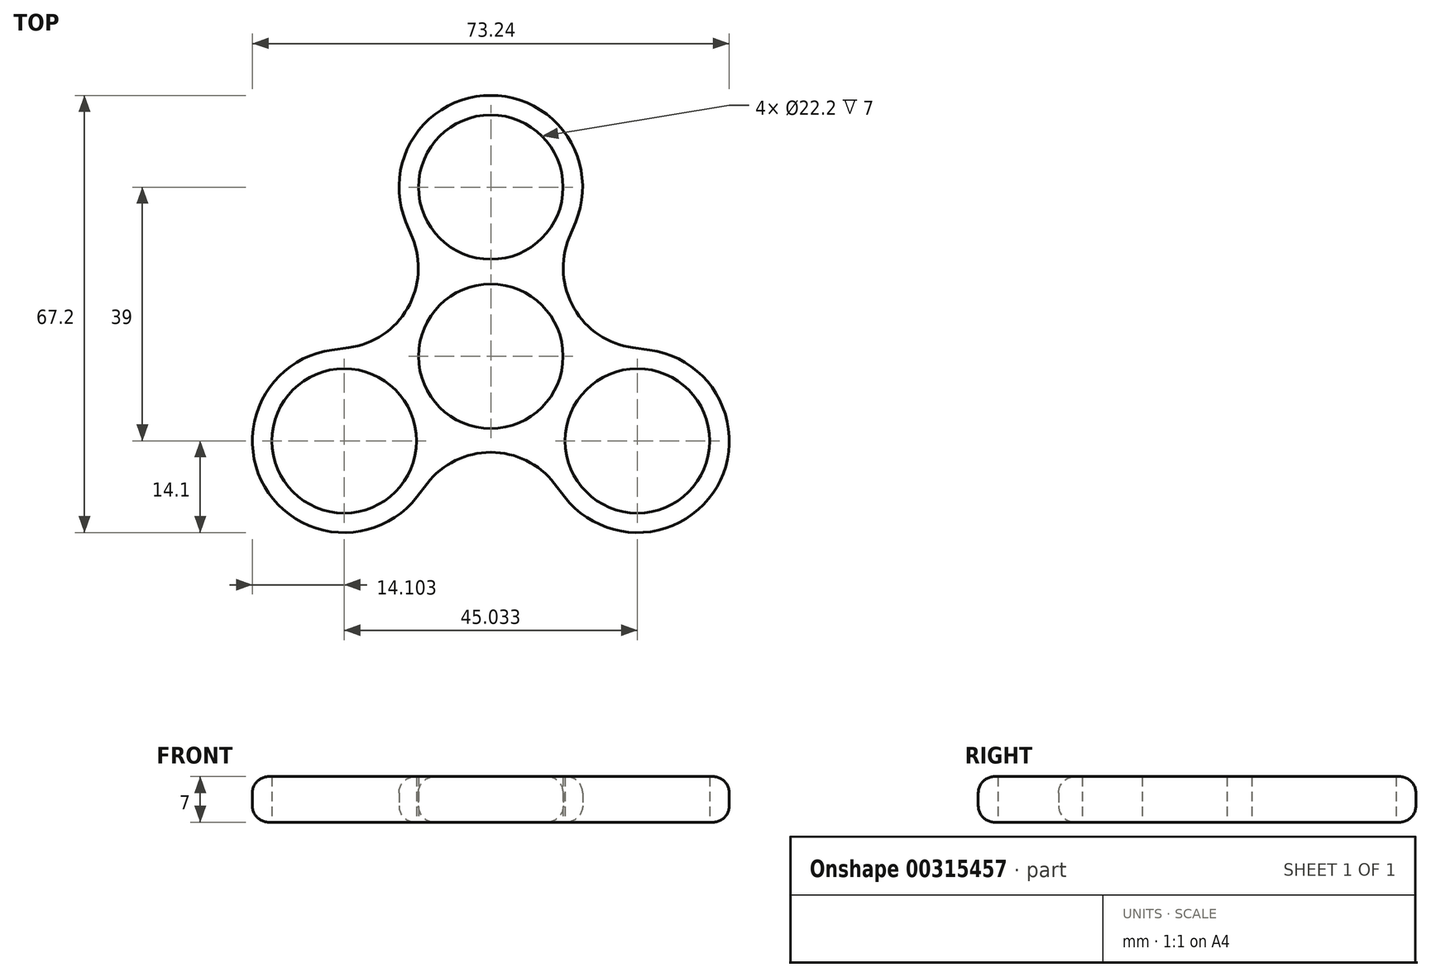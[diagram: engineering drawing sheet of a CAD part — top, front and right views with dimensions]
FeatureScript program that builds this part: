
annotation { "Feature Type Name" : "Feature", "Feature Type Description" : "" }
export const myFeature = defineFeature(function(context is Context, id is Id, definition is map)
    precondition{}
    {
        {
            var Q0;
            Q0=qCreatedBy(makeId("Top.planeOp"),FACE);
            var sketch = newSketch(context, id + "F0", { "sketchPlane" : qUnion([Q0])});
            skCircle(sketch, "E0", {"center": v(0, 0) * mm, "radius": 11.1 * mm});
            skCircle(sketch, "E1", {"center": v(0, 26) * mm, "radius": 11.1 * mm});
            skCircle(sketch, "E2", {"center": v(0, 26) * mm, "radius": 14.1 * mm});
            skLineSegment(sketch, "E3", {"start": v(0, -11.1) * mm, "end": v(-13.04, 20.64) * mm});
            skLineSegment(sketch, "E4", {"start": v(0, -11.1) * mm, "end": v(13.04, 20.64) * mm});
            skCircle(sketch, "E5.1.0", {"center": v(-22.52, -13) * mm, "radius": 14.1 * mm});
            skCircle(sketch, "E5.1.1", {"center": v(-22.52, -13) * mm, "radius": 11.1 * mm});
            skLineSegment(sketch, "E5.1.2", {"start": v(9.61, 5.55) * mm, "end": v(-11.35, -21.62) * mm});
            skLineSegment(sketch, "E5.1.3", {"start": v(9.61, 5.55) * mm, "end": v(-24.4, 0.97) * mm});
            skCircle(sketch, "E5.2.0", {"center": v(22.52, -13) * mm, "radius": 14.1 * mm});
            skCircle(sketch, "E5.2.1", {"center": v(22.52, -13) * mm, "radius": 11.1 * mm});
            skLineSegment(sketch, "E5.2.2", {"start": v(-9.61, 5.55) * mm, "end": v(24.4, 0.97) * mm});
            skLineSegment(sketch, "E5.2.3", {"start": v(-9.61, 5.55) * mm, "end": v(11.35, -21.62) * mm});
            skLineSegment(sketch, "E6", {"start": v(-12.21, 33.05) * mm, "end": v(-34.73, -5.95) * mm});
            skCircle(sketch, "E7", {"center": v(-23.47, 13.55) * mm, "radius": 12.34 * mm});
            skLineSegment(sketch, "E8", {"start": v(-22.52, -27.1) * mm, "end": v(22.52, -27.1) * mm});
            skLineSegment(sketch, "E9", {"start": v(34.73, -5.95) * mm, "end": v(12.21, 33.05) * mm});
            skCircle(sketch, "E10", {"center": v(23.47, 13.55) * mm, "radius": 12.34 * mm});
            skCircle(sketch, "E11", {"center": v(0, -27.1) * mm, "radius": 12.34 * mm});
            skSolve(sketch);
        }
        {
            var Q0;
            Q0=makeQuery(id+"F0.imprint","IMPRINT",FACE,{"disambiguationData":[TD([[makeQuery(id+"F0.imprint","IMPRINT",EDGE,{"derivedFrom":sQuery(id+"F0.wireOp",EDGE,"E1")}),-1.0]])]});
            var Q1;
            {var subQ4=sQuery(id+"F0.wireOp",EDGE,"E0");var subQ6=sQuery(id+"F0.wireOp",EDGE,"E4");var subQ8=makeQuery(id+"F0.imprint","INTERSECT",VERTEX,{"derivedFrom":[subQ4,subQ6]});Q1=makeQuery(id+"F0.imprint","IMPRINT",FACE,{"disambiguationData":[TD([[makeQuery(id+"F0.imprint","IMPRINT",EDGE,{"disambiguationData":[TD([[subQ8,-1.0]])],"derivedFrom":subQ4}),-1.0]])]});}
            var Q2;
            {var subQ1=sQuery(id+"F0.wireOp",EDGE,"E0");var subQ5=sQuery(id+"F0.wireOp",EDGE,"E3");var subQ6=makeQuery(id+"F0.imprint","INTERSECT",VERTEX,{"derivedFrom":[subQ1,subQ5]});Q2=makeQuery(id+"F0.imprint","IMPRINT",FACE,{"disambiguationData":[TD([[makeQuery(id+"F0.imprint","IMPRINT",EDGE,{"disambiguationData":[TD([[subQ6,-1.0]])],"derivedFrom":subQ5}),1.0]])]});}
            var Q3;
            {var subQ4=sQuery(id+"F0.wireOp",EDGE,"E0");var subQ6=sQuery(id+"F0.wireOp",EDGE,"E5.1.3");var subQ7=makeQuery(id+"F0.imprint","INTERSECT",VERTEX,{"derivedFrom":[subQ4,subQ6]});Q3=makeQuery(id+"F0.imprint","IMPRINT",FACE,{"disambiguationData":[TD([[makeQuery(id+"F0.imprint","IMPRINT",EDGE,{"disambiguationData":[TD([[subQ7,-1.0]])],"derivedFrom":subQ4}),-1.0]])]});}
            var Q4;
            Q4=makeQuery(id+"F0.imprint","IMPRINT",FACE,{"disambiguationData":[TD([[makeQuery(id+"F0.imprint","IMPRINT",EDGE,{"derivedFrom":sQuery(id+"F0.wireOp",EDGE,"E5.1.1")}),-1.0]])]});
            var Q5;
            {var subQ1=sQuery(id+"F0.wireOp",EDGE,"E0");var subQ5=sQuery(id+"F0.wireOp",EDGE,"E5.1.2");var subQ6=makeQuery(id+"F0.imprint","INTERSECT",VERTEX,{"derivedFrom":[subQ1,subQ5]});Q5=makeQuery(id+"F0.imprint","IMPRINT",FACE,{"disambiguationData":[TD([[makeQuery(id+"F0.imprint","IMPRINT",EDGE,{"disambiguationData":[TD([[subQ6,-1.0]])],"derivedFrom":subQ5}),1.0]])]});}
            var Q6;
            {var subQ0=sQuery(id+"F0.wireOp",EDGE,"E5.2.2");var subQ1=sQuery(id+"F0.wireOp",EDGE,"E0");var subQ2=makeQuery(id+"F0.imprint","INTERSECT",VERTEX,{"derivedFrom":[subQ1,subQ0]});Q6=makeQuery(id+"F0.imprint","IMPRINT",FACE,{"disambiguationData":[TD([[makeQuery(id+"F0.imprint","IMPRINT",EDGE,{"disambiguationData":[TD([[subQ2,1.0]])],"derivedFrom":subQ1}),-1.0]])]});}
            var Q7;
            Q7=makeQuery(id+"F0.imprint","IMPRINT",FACE,{"disambiguationData":[TD([[makeQuery(id+"F0.imprint","IMPRINT",EDGE,{"derivedFrom":sQuery(id+"F0.wireOp",EDGE,"E5.2.1")}),-1.0]])]});
            var Q8;
            {var subQ1=sQuery(id+"F0.wireOp",EDGE,"E0");var subQ5=sQuery(id+"F0.wireOp",EDGE,"E4");var subQ6=makeQuery(id+"F0.imprint","INTERSECT",VERTEX,{"derivedFrom":[subQ1,subQ5]});Q8=makeQuery(id+"F0.imprint","IMPRINT",FACE,{"disambiguationData":[TD([[makeQuery(id+"F0.imprint","IMPRINT",EDGE,{"disambiguationData":[TD([[subQ6,-1.0]])],"derivedFrom":subQ5}),-1.0]])]});}
            extrude(context, id + "F1", {"entities" : qUnion([Q0, Q1, Q2, Q3, Q4, Q5, Q6, Q7, Q8]), "depth" : 7 * mm});
        }
        {
            var Q0;
            Q0=makeQuery(id+"F1.opExtrude","CAP_EDGE",EDGE,{"disambiguationData":[OSD([sQuery(id+"F0.wireOp",EDGE,"E5.1.0")])],"isStart":false});
            var Q1;
            Q1=makeQuery(id+"F1.opExtrude","CAP_EDGE",EDGE,{"disambiguationData":[OSD([sQuery(id+"F0.wireOp",EDGE,"E5.1.0")])],"isStart":true});
            fillet(context, id + "F2", {"entities" : qUnion([Q0, Q1]), "radius" : 2.5 * mm, "tangentPropagation" : true, "allowEdgeOverflow" : false});
        }
    });
